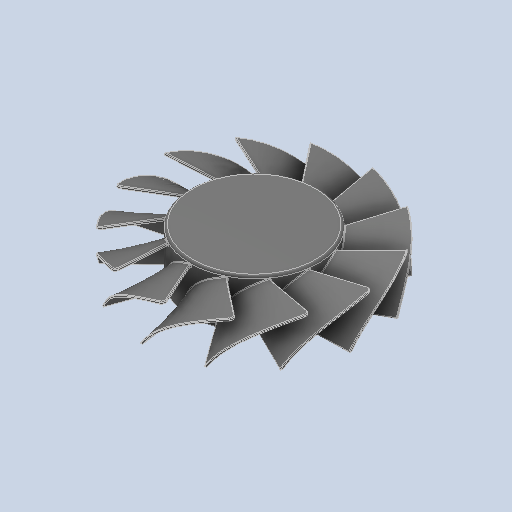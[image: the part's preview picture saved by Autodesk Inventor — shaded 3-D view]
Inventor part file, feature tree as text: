
AUTODESK INVENTOR PART (.ipt)
format: ipt  version: 2024.3 (Build 283343000, 343)  size: 1,284,608 bytes
history: native  units: in
note: dims shown in document units (in); Inventor stores cm internally (conversion verified against a paired STEP export)
features: fillet x1
ambient origin geometry x8: Origin, YZ Plane, XZ Plane, XY Plane, X Axis, Y Axis, Z Axis, Center Point
bodies: Solid1 (feature_tree)
feature tree (1):
  fillet  "Fillet10"  [1 undecoded]
note: 1 required parameter value undecoded (feature->parameter linkage not recoverable at this tier; creation-order binding heuristic only, values carry confidence <= 0.55)
